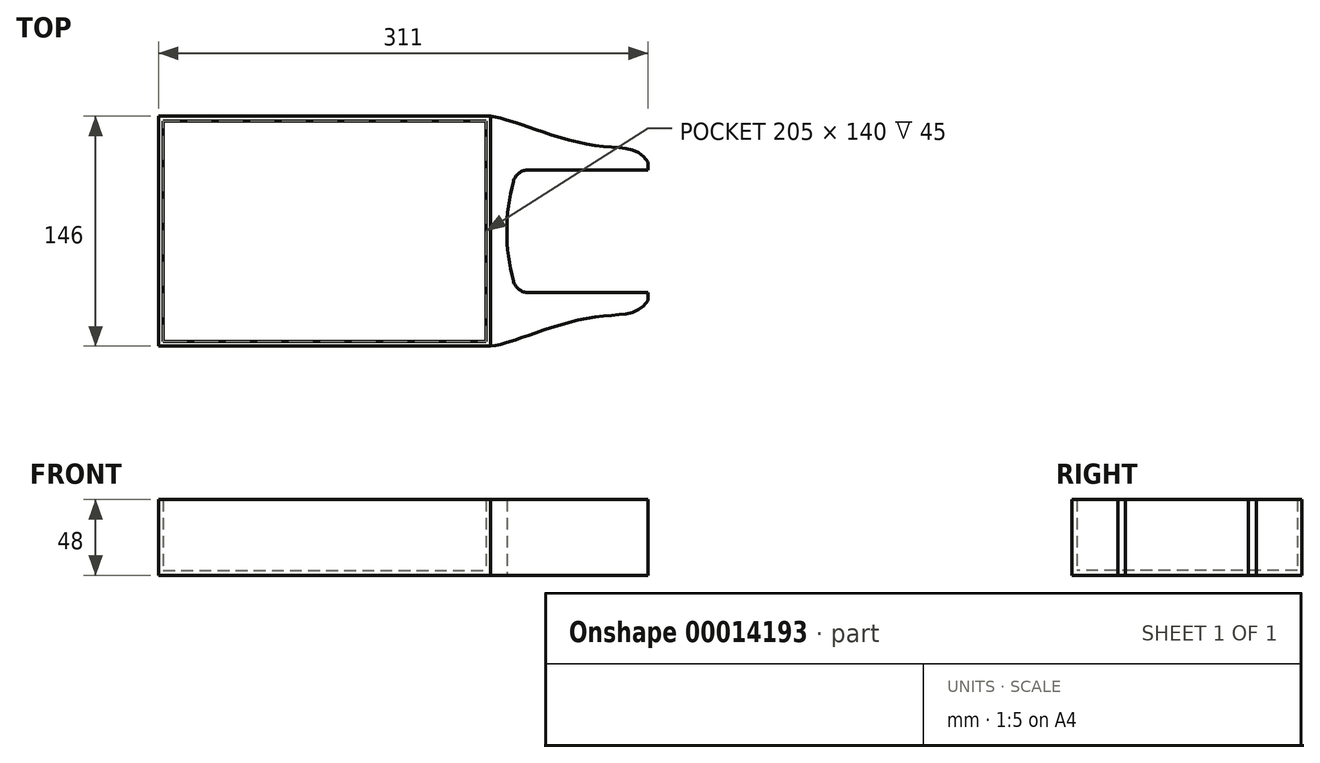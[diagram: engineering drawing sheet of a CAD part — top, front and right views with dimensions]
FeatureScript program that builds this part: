
annotation { "Feature Type Name" : "Feature", "Feature Type Description" : "" }
export const myFeature = defineFeature(function(context is Context, id is Id, definition is map)
    precondition{}
    {
        {
            var Q0;
            Q0=qCreatedBy(makeId("Top.planeOp"),FACE);
            var sketch = newSketch(context, id + "F0", { "sketchPlane" : qUnion([Q0])});
            skLineSegment(sketch, "E0.bottom", {"start": v(-175.14, 0) * mm, "end": v(29.86, 0) * mm});
            skLineSegment(sketch, "E0.top", {"start": v(-175.14, -140) * mm, "end": v(29.86, -140) * mm});
            skLineSegment(sketch, "E0.left", {"start": v(-175.14, 0) * mm, "end": v(-175.14, -140) * mm});
            skLineSegment(sketch, "E0.right", {"start": v(29.86, 0) * mm, "end": v(29.86, -140) * mm});
            skSolve(sketch);
        }
        {
            var Q0;
            Q0=makeQuery(id+"F0.imprint","IMPRINT",FACE,{"disambiguationData":[TD([[makeQuery(id+"F0.imprint","IMPRINT",EDGE,{"derivedFrom":sQuery(id+"F0.wireOp",EDGE,"E0.bottom")}),-1.0]])]});
            extrude(context, id + "F1", {"entities" : qUnion([Q0]), "depth" : 45 * mm});
        }
        {
            var Q0;
            Q0=makeQuery(id+"F1.opExtrude","CAP_FACE",FACE,{"disambiguationData":[OSD([sQuery(id+"F0.wireOp",EDGE,"E0.bottom"),sQuery(id+"F0.wireOp",EDGE,"E0.top"),sQuery(id+"F0.wireOp",EDGE,"E0.left"),sQuery(id+"F0.wireOp",EDGE,"E0.right")])],"isStart":false});
            shell(context, id + "F2", {"entities" : qUnion([Q0]), "thickness" : 3 * mm, "oppositeDirection" : true});
        }
        {
            var Q0;
            Q0=makeQuery(id+"F1.opExtrude","CAP_FACE",FACE,{"disambiguationData":[OSD([sQuery(id+"F0.wireOp",EDGE,"E0.bottom"),sQuery(id+"F0.wireOp",EDGE,"E0.top"),sQuery(id+"F0.wireOp",EDGE,"E0.left"),sQuery(id+"F0.wireOp",EDGE,"E0.right")])],"isStart":true});
            var sketch = newSketch(context, id + "F3", { "sketchPlane" : qUnion([Q0])});
            skLineSegment(sketch, "E1", {"start": v(32.86, 70) * mm, "end": v(221.11, 70) * mm, "construction": true});
            skLineSegment(sketch, "E2", {"start": v(56.88, 109) * mm, "end": v(132.86, 109) * mm});
            skLineSegment(sketch, "E3", {"start": v(132.86, 109) * mm, "end": v(132.86, 114) * mm});
            skFitSpline(sketch, "E4", {"points": [v(132.86, 114) * mm, v(101.2, 124.15) * mm, v(52.16, 137.76) * mm, v(32.86, 143) * mm], "startDerivative": vector(-60.97, 92.83) * mm, "endDerivative": vector(-75.59, 9.35) * mm});
            skLineSegment(sketch, "E5.MirrorCS", {"start": v(56.88, 31) * mm, "end": v(132.86, 31) * mm});
            skLineSegment(sketch, "E6.MirrorCS", {"start": v(132.86, 31) * mm, "end": v(132.86, 26) * mm});
            skFitSpline(sketch, "E7.MirrorCS", {"points": [v(132.86, 26) * mm, v(101.2, 15.85) * mm, v(52.16, 2.24) * mm, v(32.86, -3) * mm], "startDerivative": vector(-60.97, -92.83) * mm, "endDerivative": vector(-75.59, -9.35) * mm});
            skArc(sketch, "E8", {"start": v(47.22, 101.56) * mm, "mid": v(43.1, 70) * mm, "end": v(47.22, 38.44) * mm});
            skPoint(sketch, "E9.visualSharp", {"position": v(49.44, 31) * mm});
            skArc(sketch, "E9.filletArc", {"start": v(47.22, 38.44) * mm, "mid": v(50.78, 33.08) * mm, "end": v(56.88, 31) * mm});
            skPoint(sketch, "E10.visualSharp", {"position": v(49.44, 109) * mm});
            skArc(sketch, "E10.filletArc", {"start": v(56.88, 109) * mm, "mid": v(50.78, 106.92) * mm, "end": v(47.22, 101.56) * mm});
            skSolve(sketch);
        }
        {
            var Q0;
            Q0 = qSketchRegion(id + "F3", true);
            var Q1;
            {var subQ1=sQuery(id+"F3.wireOp",EDGE,"E2");Q1=makeQuery(id+"F3.imprint","IMPRINT",FACE,{"disambiguationData":[TD([[makeQuery(id+"F3.imprint","IMPRINT",EDGE,{"derivedFrom":subQ1}),1.0]])]});}
            var Q2;
            {var subQ1=sQuery(id+"F3.wireOp",EDGE,"E5.MirrorCS");Q2=makeQuery(id+"F3.imprint","IMPRINT",FACE,{"disambiguationData":[TD([[makeQuery(id+"F3.imprint","IMPRINT",EDGE,{"derivedFrom":subQ1}),-1.0]])]});}
            extrude(context, id + "F4", {"entities" : qUnion([Q0, Q1, Q2]), "oppositeDirection" : true, "depth" : 48 * mm});
        }
    });
